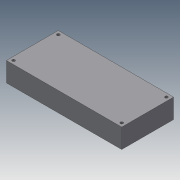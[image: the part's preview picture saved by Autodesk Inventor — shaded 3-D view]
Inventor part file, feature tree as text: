
AUTODESK INVENTOR PART (.ipt)
format: ipt  version: 2014 SP1 (Build 180222100, 222)  size: 85,504 bytes
history: native  units: in
note: dims shown in document units (in); Inventor stores cm internally (conversion verified against a paired STEP export)
features: extrude x1, sketch x1
ambient origin geometry x8: Origin, YZ Plane, XZ Plane, XY Plane, X Axis, Y Axis, Z Axis, Center Point
bodies: Solid1 (feature_tree)
feature tree (2):
  extrude  "Extrusion1"  Depth=1.4173in
  sketch  "Sketch1"  dims[d0=3.1496in d1=1.4173in d2=0.7087in d3=1.5748in d4=0.0787in d5=2.9528in d6=1.2205in d7=1.4764in d8=0.6102in d9=0.0787in d10=0.0787in d11=0.0787in d12=0.5315in d13=0.0in]
